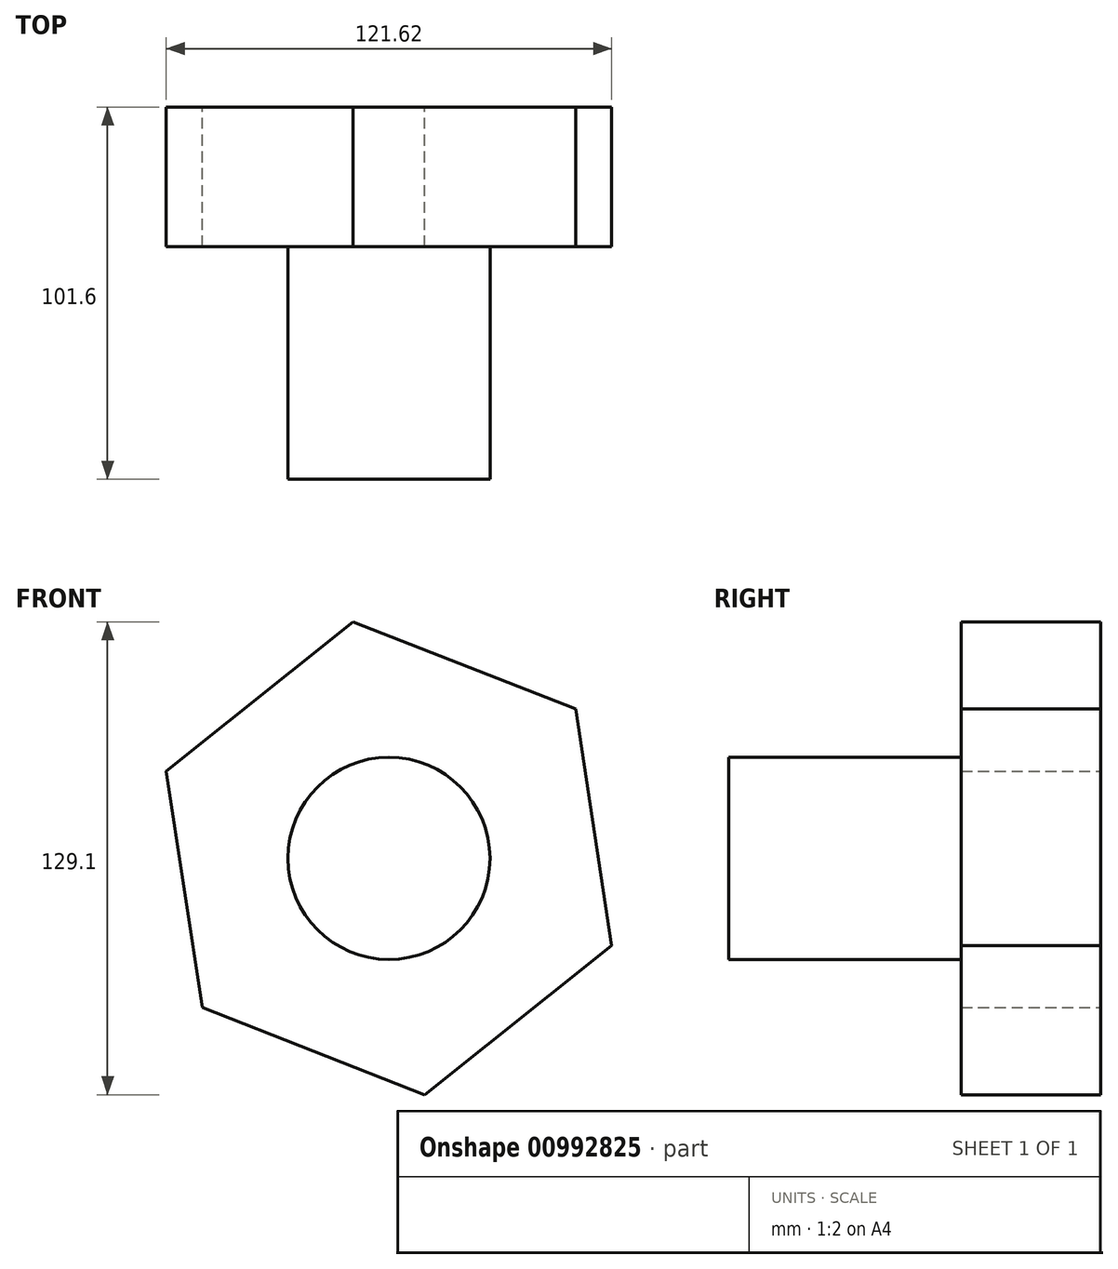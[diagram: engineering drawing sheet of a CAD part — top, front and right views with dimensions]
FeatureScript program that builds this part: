
annotation { "Feature Type Name" : "Feature", "Feature Type Description" : "" }
export const myFeature = defineFeature(function(context is Context, id is Id, definition is map)
    precondition{}
    {
        {
            var Q0;
            Q0=qCreatedBy(makeId("Front.planeOp"),FACE);
            var sketch = newSketch(context, id + "F0", { "sketchPlane" : qUnion([Q0])});
            skCircle(sketch, "E0.cCircle", {"center": v(0, 0) * mm, "radius": 56.55 * mm, "construction": true});
            skLineSegment(sketch, "E0.0", {"start": v(-9.8, 64.55) * mm, "end": v(51, 40.77) * mm});
            skLineSegment(sketch, "E0.1", {"start": v(51, 40.77) * mm, "end": v(60.8, -23.79) * mm});
            skLineSegment(sketch, "E0.2", {"start": v(60.8, -23.79) * mm, "end": v(9.8, -64.55) * mm});
            skLineSegment(sketch, "E0.3", {"start": v(9.8, -64.55) * mm, "end": v(-51, -40.77) * mm});
            skLineSegment(sketch, "E0.4", {"start": v(-51, -40.77) * mm, "end": v(-60.8, 23.79) * mm});
            skLineSegment(sketch, "E0.5", {"start": v(-60.8, 23.79) * mm, "end": v(-9.8, 64.55) * mm});
            skPoint(sketch, "E0.0.midPoint", {"position": v(20.6, 52.66) * mm});
            skSolve(sketch);
        }
        {
            var Q0;
            Q0 = qSketchRegion(id + "F0", true);
            extrude(context, id + "F1", {"entities" : qUnion([Q0]), "depth" : 38.1 * mm, "offsetDistance" : 25.4 * mm});
        }
        {
            var Q0;
            Q0=makeQuery(id+"F1.opExtrude","CAP_FACE",FACE,{"disambiguationData":[OSD([sQuery(id+"F0.wireOp",EDGE,"E0.0"),sQuery(id+"F0.wireOp",EDGE,"E0.1"),sQuery(id+"F0.wireOp",EDGE,"E0.2"),sQuery(id+"F0.wireOp",EDGE,"E0.3"),sQuery(id+"F0.wireOp",EDGE,"E0.4"),sQuery(id+"F0.wireOp",EDGE,"E0.5")])],"isStart":false});
            var sketch = newSketch(context, id + "F2", { "sketchPlane" : qUnion([Q0])});
            skCircle(sketch, "E1", {"center": v(0, 0) * mm, "radius": 27.6 * mm});
            skSolve(sketch);
        }
        {
            var Q0;
            Q0=makeQuery(id+"F2.imprint","IMPRINT",FACE,{"disambiguationData":[TD([[makeQuery(id+"F2.imprint","IMPRINT",EDGE,{"derivedFrom":sQuery(id+"F2.wireOp",EDGE,"E1")}),1.0]])]});
            var Q1;
            Q1 = qSketchRegion(id + "F2", true);
            extrude(context, id + "F3", {"entities" : qUnion([Q0, Q1]), "operationType" : NewBodyOperationType.ADD, "depth" : 63.5 * mm, "offsetDistance" : 25.4 * mm});
        }
    });
